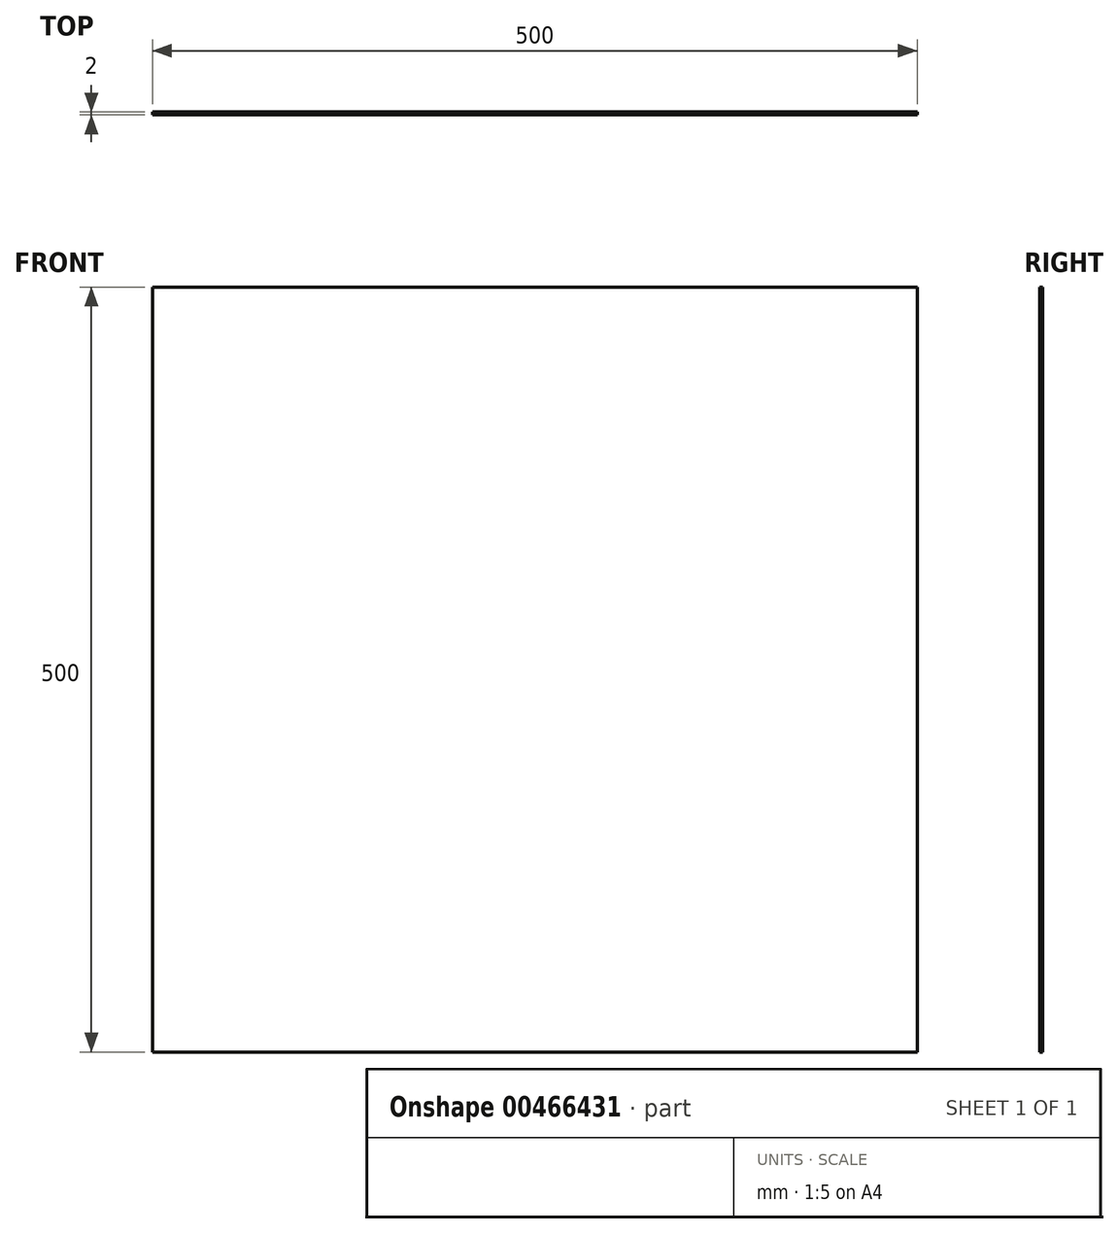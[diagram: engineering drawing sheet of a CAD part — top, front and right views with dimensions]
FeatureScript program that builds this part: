
annotation { "Feature Type Name" : "Feature", "Feature Type Description" : "" }
export const myFeature = defineFeature(function(context is Context, id is Id, definition is map)
    precondition{}
    {
        {
            var Q0;
            Q0=qCreatedBy(makeId("Front.planeOp"),FACE);
            var sketch = newSketch(context, id + "F0", { "sketchPlane" : qUnion([Q0])});
            skLineSegment(sketch, "E0.bottom", {"start": v(250, -250) * mm, "end": v(-250, -250) * mm});
            skLineSegment(sketch, "E0.top", {"start": v(250, 250) * mm, "end": v(-250, 250) * mm});
            skLineSegment(sketch, "E0.left", {"start": v(250, -250) * mm, "end": v(250, 250) * mm});
            skLineSegment(sketch, "E0.right", {"start": v(-250, -250) * mm, "end": v(-250, 250) * mm});
            skPoint(sketch, "E0.middle", {"position": v(0, 0) * mm});
            skSolve(sketch);
        }
        {
            var Q0;
            Q0=makeQuery(id+"F0.imprint","IMPRINT",FACE,{"disambiguationData":[TD([[makeQuery(id+"F0.imprint","IMPRINT",EDGE,{"derivedFrom":sQuery(id+"F0.wireOp",EDGE,"E0.bottom")}),-1.0]])]});
            extrude(context, id + "F1", {"entities" : qUnion([Q0]), "depth" : 2 * mm});
        }
    });
